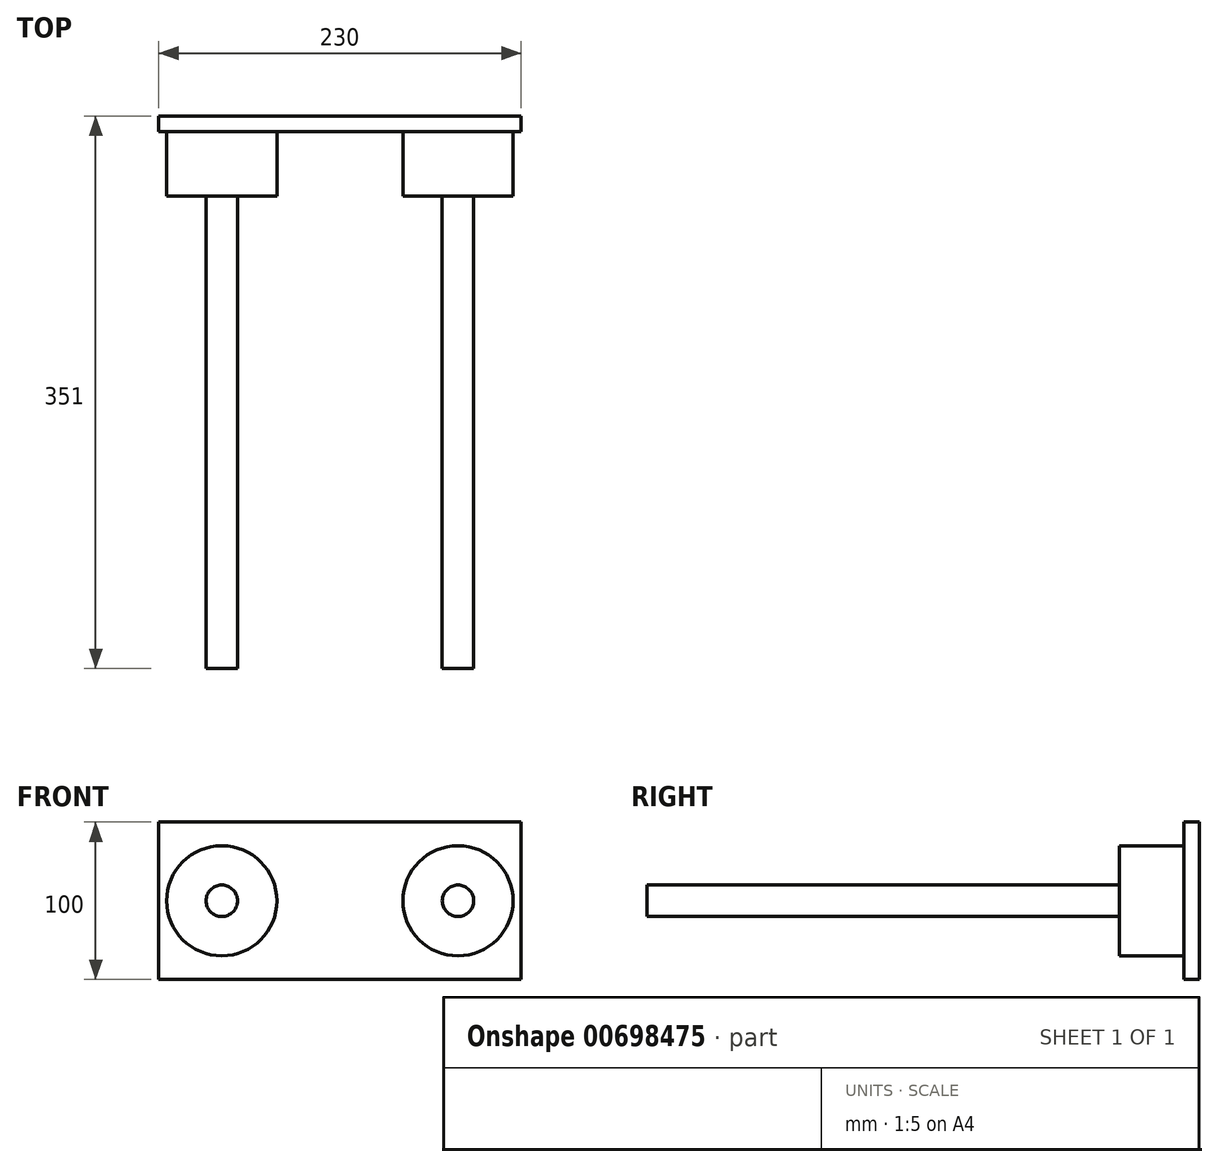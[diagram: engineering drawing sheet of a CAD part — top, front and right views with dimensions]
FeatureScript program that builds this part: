
annotation { "Feature Type Name" : "Feature", "Feature Type Description" : "" }
export const myFeature = defineFeature(function(context is Context, id is Id, definition is map)
    precondition{}
    {
        {
            var Q0;
            Q0=qCreatedBy(makeId("Front.planeOp"),FACE);
            var sketch = newSketch(context, id + "F0", { "sketchPlane" : qUnion([Q0])});
            skLineSegment(sketch, "E0.bottom", {"start": v(-115, 50) * mm, "end": v(115, 50) * mm});
            skLineSegment(sketch, "E0.top", {"start": v(-115, -50) * mm, "end": v(115, -50) * mm});
            skLineSegment(sketch, "E0.left", {"start": v(-115, 50) * mm, "end": v(-115, -50) * mm});
            skLineSegment(sketch, "E0.right", {"start": v(115, 50) * mm, "end": v(115, -50) * mm});
            skSolve(sketch);
        }
        {
            var Q0;
            Q0=makeQuery(id+"F0.imprint","IMPRINT",FACE,{"disambiguationData":[TD([[makeQuery(id+"F0.imprint","IMPRINT",EDGE,{"derivedFrom":sQuery(id+"F0.wireOp",EDGE,"E0.bottom")}),-1.0]])]});
            extrude(context, id + "F1", {"entities" : qUnion([Q0]), "depth" : 10 * mm, "offsetDistance" : 25 * mm});
        }
        {
            var Q0;
            Q0=makeQuery(id+"F1.opExtrude","CAP_FACE",FACE,{"disambiguationData":[OSD([sQuery(id+"F0.wireOp",EDGE,"E0.bottom"),sQuery(id+"F0.wireOp",EDGE,"E0.top"),sQuery(id+"F0.wireOp",EDGE,"E0.left"),sQuery(id+"F0.wireOp",EDGE,"E0.right")])],"isStart":false});
            var sketch = newSketch(context, id + "F2", { "sketchPlane" : qUnion([Q0])});
            skCircle(sketch, "E1", {"center": v(-75, 0) * mm, "radius": 35 * mm});
            skCircle(sketch, "E2", {"center": v(75, 0) * mm, "radius": 35 * mm});
            skSolve(sketch);
        }
        {
            var Q0;
            Q0=makeQuery(id+"F2.imprint","IMPRINT",FACE,{"disambiguationData":[TD([[makeQuery(id+"F2.imprint","IMPRINT",EDGE,{"derivedFrom":sQuery(id+"F2.wireOp",EDGE,"E1")}),1.0]])]});
            var Q1;
            Q1=makeQuery(id+"F2.imprint","IMPRINT",FACE,{"disambiguationData":[TD([[makeQuery(id+"F2.imprint","IMPRINT",EDGE,{"derivedFrom":sQuery(id+"F2.wireOp",EDGE,"E2")}),1.0]])]});
            var Q2;
            Q2=sQuery(id+"F2.wireOp",EDGE,"E1");
            var Q3;
            Q3=sQuery(id+"F2.wireOp",EDGE,"E2");
            extrude(context, id + "F3", {"entities" : qUnion([Q0, Q1]), "operationType" : NewBodyOperationType.ADD, "surfaceEntities" : qUnion([Q2, Q3]), "depth" : 41 * mm, "offsetDistance" : 25 * mm});
        }
        {
            var Q0;
            Q0=makeQuery(id+"F3.opExtrude","CAP_FACE",FACE,{"disambiguationData":[OSD([sQuery(id+"F2.wireOp",EDGE,"E1")])],"isStart":false});
            var sketch = newSketch(context, id + "F4", { "sketchPlane" : qUnion([Q0])});
            skCircle(sketch, "E3", {"center": v(-75, 0) * mm, "radius": 10 * mm});
            skCircle(sketch, "E4", {"center": v(75, 0) * mm, "radius": 10 * mm});
            skSolve(sketch);
        }
        {
            var Q0;
            Q0=makeQuery(id+"F4.imprint","IMPRINT",FACE,{"disambiguationData":[TD([[makeQuery(id+"F4.imprint","IMPRINT",EDGE,{"derivedFrom":sQuery(id+"F4.wireOp",EDGE,"E3")}),1.0]])]});
            var Q1;
            Q1=makeQuery(id+"F4.imprint","IMPRINT",FACE,{"disambiguationData":[TD([[makeQuery(id+"F4.imprint","IMPRINT",EDGE,{"derivedFrom":sQuery(id+"F4.wireOp",EDGE,"E4")}),1.0]])]});
            var Q2;
            Q2=sQuery(id+"F4.wireOp",EDGE,"E4");
            var Q3;
            Q3=sQuery(id+"F4.wireOp",EDGE,"E3");
            extrude(context, id + "F5", {"entities" : qUnion([Q0, Q1]), "operationType" : NewBodyOperationType.ADD, "surfaceEntities" : qUnion([Q2, Q3]), "depth" : 300 * mm, "offsetDistance" : 25 * mm});
        }
    });
